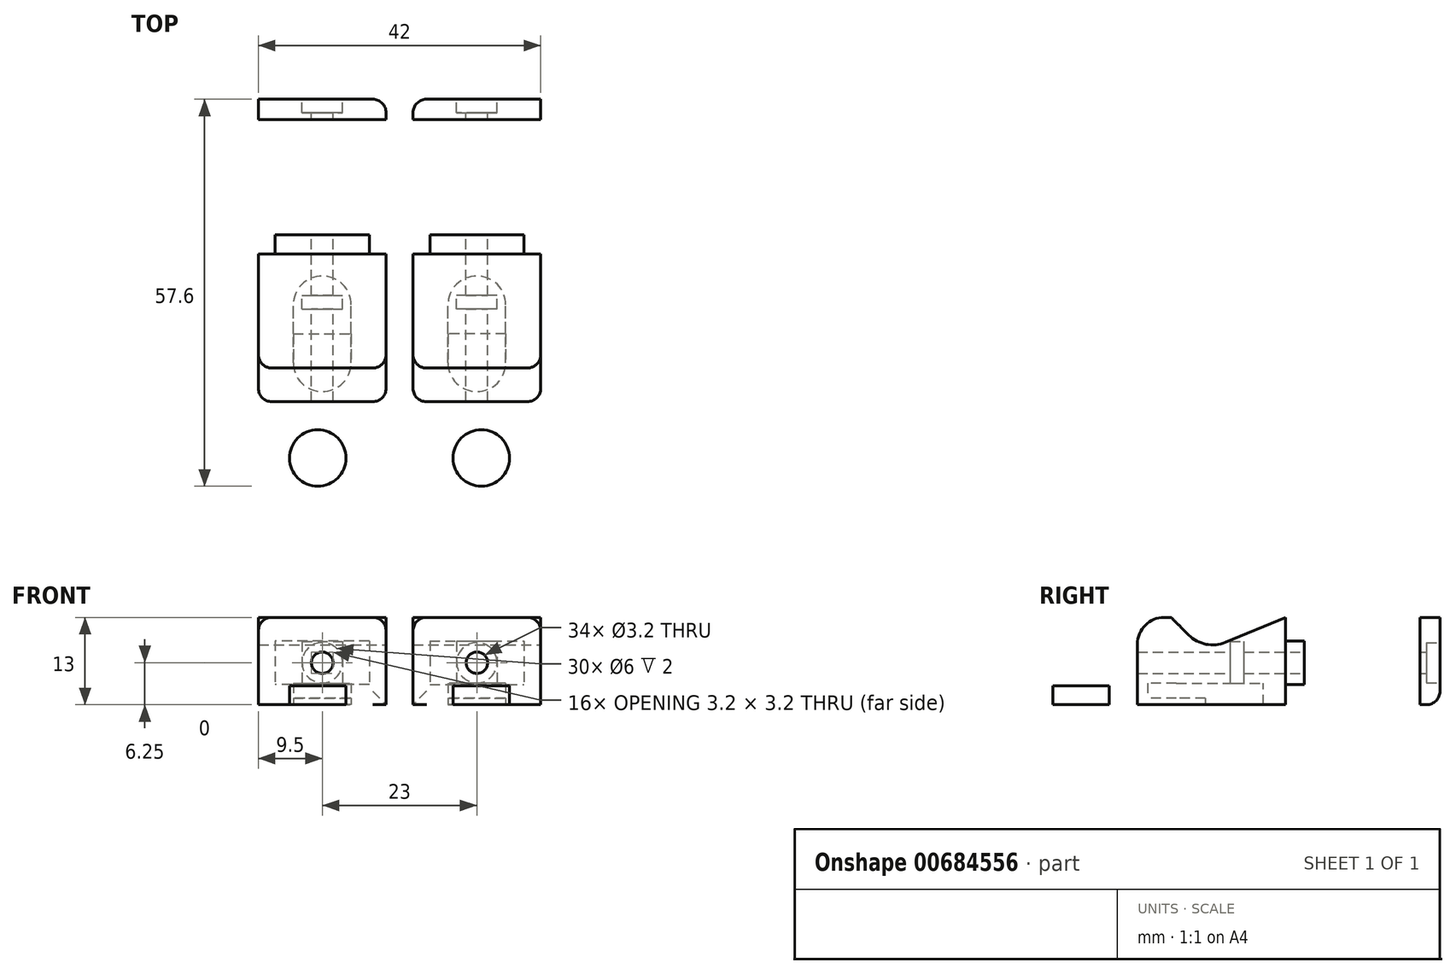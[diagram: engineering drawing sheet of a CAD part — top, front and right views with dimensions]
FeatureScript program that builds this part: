
annotation { "Feature Type Name" : "Feature", "Feature Type Description" : "" }
export const myFeature = defineFeature(function(context is Context, id is Id, definition is map)
    precondition{}
    {
        {
            var Q0;
            Q0=qCreatedBy(makeId("Top.planeOp"),FACE);
            var sketch = newSketch(context, id + "F0", { "sketchPlane" : qUnion([Q0])});
            skLineSegment(sketch, "E0.bottom", {"start": v(-2, 0) * mm, "end": v(-21, 0) * mm});
            skLineSegment(sketch, "E0.top", {"start": v(-2, -22) * mm, "end": v(-21, -22) * mm});
            skLineSegment(sketch, "E0.left", {"start": v(-2, 0) * mm, "end": v(-2, -22) * mm});
            skLineSegment(sketch, "E0.right", {"start": v(-21, 0) * mm, "end": v(-21, -22) * mm});
            skSolve(sketch);
        }
        {
            var Q0;
            Q0=makeQuery(id+"F0.imprint","IMPRINT",FACE,{"disambiguationData":[TD([[makeQuery(id+"F0.imprint","IMPRINT",EDGE,{"derivedFrom":sQuery(id+"F0.wireOp",EDGE,"E0.bottom")}),1.0]])]});
            extrude(context, id + "F1", {"entities" : qUnion([Q0]), "depth" : 13 * mm, "offsetDistance" : 25 * mm});
        }
        {
            var Q0;
            Q0=makeQuery(id+"F1.opExtrude","SWEPT_FACE",FACE,{"disambiguationData":[OSD([sQuery(id+"F0.wireOp",EDGE,"E0.right")])]});
            var sketch = newSketch(context, id + "F2", { "sketchPlane" : qUnion([Q0])});
            skLineSegment(sketch, "E1", {"start": v(0, 13) * mm, "end": v(12, 8) * mm});
            skLineSegment(sketch, "E2", {"start": v(12, 8) * mm, "end": v(17, 13) * mm});
            skSolve(sketch);
        }
        {
            var Q0;
            {var subQ0=sQuery(id+"F2.wireOp",EDGE,"E1");Q0=makeQuery(id+"F2.imprint","IMPRINT",FACE,{"disambiguationData":[TD([[makeQuery(id+"F2.imprint","IMPRINT",EDGE,{"derivedFrom":subQ0}),1.0]])]});}
            extrude(context, id + "F3", {"entities" : qUnion([Q0]), "operationType" : NewBodyOperationType.REMOVE, "endBound" : BoundingType.THROUGH_ALL, "oppositeDirection" : true, "depth" : 25 * mm, "offsetDistance" : 25 * mm});
        }
        {
            var Q0;
            Q0=makeQuery(id+"F3.boolean.opBoolean","COPY",EDGE,{"derivedFrom":makeQuery(id+"F3.opExtrude","SWEPT_EDGE",EDGE,{"disambiguationData":[OSD([sQuery(id+"F2.wireOp",EDGE,"E1"),sQuery(id+"F2.wireOp",EDGE,"E2")])]})});
            fillet(context, id + "F4", {"entities" : qUnion([Q0]), "radius" : 5 * mm, "tangentPropagation" : true, "allowEdgeOverflow" : false});
        }
        {
            var Q0;
            Q0=makeQuery(id+"F3.boolean.opBoolean","COPY",EDGE,{"derivedFrom":makeQuery(id+"F3.opExtrude","SWEPT_EDGE",EDGE,{"disambiguationData":[OSD([sQuery(id+"F0.wireOp",EDGE,"E0.right"),sQuery(id+"F2.wireOp",EDGE,"E2")])]})});
            var Q1;
            Q1=makeQuery(id+"F1.opExtrude","CAP_EDGE",EDGE,{"disambiguationData":[OSD([sQuery(id+"F0.wireOp",EDGE,"E0.top")])],"isStart":false});
            fillet(context, id + "F5", {"entities" : qUnion([Q0, Q1]), "radius" : 4 * mm, "tangentPropagation" : true, "allowEdgeOverflow" : false});
        }
        {
            var Q0;
            Q0=makeQuery(id+"F1.opExtrude","SWEPT_EDGE",EDGE,{"disambiguationData":[OSD([sQuery(id+"F0.wireOp",EDGE,"E0.top"),sQuery(id+"F0.wireOp",EDGE,"E0.right")])]});
            var Q1;
            {var subQ0=sQuery(id+"F0.wireOp",EDGE,"E0.right");Q1=makeQuery(id+"F5.opFillet","BLEND_EDGE",EDGE,{"blendedFrom":[makeQuery(id+"F3.boolean.opBoolean","COPY",EDGE,{"derivedFrom":makeQuery(id+"F3.opExtrude","SWEPT_EDGE",EDGE,{"disambiguationData":[OSD([subQ0,sQuery(id+"F2.wireOp",EDGE,"E2")])]})}),makeQuery(id+"F1.opExtrude","SWEPT_FACE",FACE,{"disambiguationData":[OSD([subQ0])]})],"blendedInto":[makeQuery(id+"F1.opExtrude","SWEPT_FACE",FACE,{"disambiguationData":[OSD([subQ0])]})]});}
            var Q2;
            Q2=makeQuery(id+"F5.opFillet","BLEND_EDGE",EDGE,{"blendedFrom":[makeQuery(id+"F1.opExtrude","CAP_EDGE",EDGE,{"disambiguationData":[OSD([sQuery(id+"F0.wireOp",EDGE,"E0.top")])],"isStart":false}),makeQuery(id+"F1.opExtrude","SWEPT_FACE",FACE,{"disambiguationData":[OSD([sQuery(id+"F0.wireOp",EDGE,"E0.left")])]})],"blendedInto":[makeQuery(id+"F1.opExtrude","SWEPT_FACE",FACE,{"disambiguationData":[OSD([sQuery(id+"F0.wireOp",EDGE,"E0.left")])]})]});
            var Q3;
            Q3=makeQuery(id+"F1.opExtrude","SWEPT_EDGE",EDGE,{"disambiguationData":[OSD([sQuery(id+"F0.wireOp",EDGE,"E0.top"),sQuery(id+"F0.wireOp",EDGE,"E0.left")])]});
            var Q4;
            Q4=makeQuery(id+"F5.opFillet","BLEND_EDGE",EDGE,{"blendedFrom":[makeQuery(id+"F3.boolean.opBoolean","COPY",EDGE,{"derivedFrom":makeQuery(id+"F3.opExtrude","SWEPT_EDGE",EDGE,{"disambiguationData":[OSD([sQuery(id+"F0.wireOp",EDGE,"E0.right"),sQuery(id+"F2.wireOp",EDGE,"E2")])]})}),makeQuery(id+"F1.opExtrude","SWEPT_FACE",FACE,{"disambiguationData":[OSD([sQuery(id+"F0.wireOp",EDGE,"E0.left")])]})],"blendedInto":[makeQuery(id+"F1.opExtrude","SWEPT_FACE",FACE,{"disambiguationData":[OSD([sQuery(id+"F0.wireOp",EDGE,"E0.left")])]})]});
            fillet(context, id + "F6", {"entities" : qUnion([Q0, Q1, Q2, Q3, Q4]), "radius" : 2 * mm, "tangentPropagation" : true, "allowEdgeOverflow" : false});
        }
        {
            var Q0;
            Q0=makeQuery(id+"F1.opExtrude","SWEPT_FACE",FACE,{"disambiguationData":[OSD([sQuery(id+"F0.wireOp",EDGE,"E0.bottom")])]});
            extrude(context, id + "F7", {"entities" : qUnion([Q0]), "depth" : 3 * mm, "offsetDistance" : 25 * mm});
        }
        {
            var Q0;
            Q0=makeQuery(id+"F7.opExtrude","SWEPT_BODY",BODY,{"disambiguationData":[OSD([sQuery(id+"F0.wireOp",EDGE,"E0.bottom")])]});
            transform(context, id + "F8", {"entities" : qUnion([Q0]), "transformType" : TransformType.TRANSLATION_3D, "dx" : 0 * mm, "dy" : 20 * mm, "dz" : 0 * mm, "makeCopy" : false});
        }
        {
            var Q0;
            Q0=makeQuery(id+"F1.opExtrude","SWEPT_FACE",FACE,{"disambiguationData":[OSD([sQuery(id+"F0.wireOp",EDGE,"E0.bottom")])]});
            var sketch = newSketch(context, id + "F9", { "sketchPlane" : qUnion([Q0])});
            skLineSegment(sketch, "E3.bottom", {"start": v(4.5, 9.5) * mm, "end": v(18.5, 9.5) * mm});
            skLineSegment(sketch, "E3.top", {"start": v(4.5, 3) * mm, "end": v(18.5, 3) * mm});
            skLineSegment(sketch, "E3.left", {"start": v(4.5, 9.5) * mm, "end": v(4.5, 3) * mm});
            skLineSegment(sketch, "E3.right", {"start": v(18.5, 9.5) * mm, "end": v(18.5, 3) * mm});
            skSolve(sketch);
        }
        {
            var Q0;
            Q0=makeQuery(id+"F9.imprint","IMPRINT",FACE,{"disambiguationData":[TD([[makeQuery(id+"F9.imprint","IMPRINT",EDGE,{"derivedFrom":sQuery(id+"F9.wireOp",EDGE,"E3.bottom")}),-1.0]])]});
            extrude(context, id + "F10", {"entities" : qUnion([Q0]), "operationType" : NewBodyOperationType.ADD, "depth" : 2.8 * mm, "offsetDistance" : 25 * mm});
        }
        {
            var Q0;
            Q0=makeQuery(id+"F10.opExtrude","CAP_FACE",FACE,{"disambiguationData":[OSD([sQuery(id+"F9.wireOp",EDGE,"E3.bottom"),sQuery(id+"F9.wireOp",EDGE,"E3.top"),sQuery(id+"F9.wireOp",EDGE,"E3.left"),sQuery(id+"F9.wireOp",EDGE,"E3.right")])],"isStart":false});
            var sketch = newSketch(context, id + "F11", { "sketchPlane" : qUnion([Q0])});
            skCircle(sketch, "E4", {"center": v(11.5, 6.25) * mm, "radius": 1.6 * mm});
            skSolve(sketch);
        }
        {
            var Q0;
            Q0=makeQuery(id+"F11.imprint","IMPRINT",FACE,{"disambiguationData":[TD([[makeQuery(id+"F11.imprint","IMPRINT",EDGE,{"derivedFrom":sQuery(id+"F11.wireOp",EDGE,"E4")}),1.0]])]});
            extrude(context, id + "F12", {"entities" : qUnion([Q0]), "operationType" : NewBodyOperationType.REMOVE, "oppositeDirection" : true, "depth" : 20 * mm, "offsetDistance" : 25 * mm});
        }
        {
            var Q0;
            Q0=makeQuery(id+"F1.opExtrude","CAP_FACE",FACE,{"disambiguationData":[OSD([sQuery(id+"F0.wireOp",EDGE,"E0.bottom"),sQuery(id+"F0.wireOp",EDGE,"E0.top"),sQuery(id+"F0.wireOp",EDGE,"E0.left"),sQuery(id+"F0.wireOp",EDGE,"E0.right")])],"isStart":true});
            var sketch = newSketch(context, id + "F13", { "sketchPlane" : qUnion([Q0])});
            skLineSegment(sketch, "E5.bottom", {"start": v(-15.8, 20.5) * mm, "end": v(-7.2, 20.5) * mm});
            skLineSegment(sketch, "E5.top", {"start": v(-15.8, 3.3) * mm, "end": v(-7.2, 3.3) * mm});
            skLineSegment(sketch, "E5.left", {"start": v(-15.8, 20.5) * mm, "end": v(-15.8, 3.3) * mm});
            skLineSegment(sketch, "E5.right", {"start": v(-7.2, 20.5) * mm, "end": v(-7.2, 3.3) * mm});
            skSolve(sketch);
        }
        {
            var Q0;
            Q0=makeQuery(id+"F13.imprint","IMPRINT",FACE,{"disambiguationData":[TD([[makeQuery(id+"F13.imprint","IMPRINT",EDGE,{"derivedFrom":sQuery(id+"F13.wireOp",EDGE,"E5.bottom")}),-1.0]])]});
            extrude(context, id + "F14", {"entities" : qUnion([Q0]), "operationType" : NewBodyOperationType.REMOVE, "oppositeDirection" : true, "depth" : 3.2 * mm, "offsetDistance" : 25 * mm});
        }
        {
            var Q0;
            Q0=makeQuery(id+"F14.boolean.opBoolean","COPY",FACE,{"derivedFrom":makeQuery(id+"F14.opExtrude","SWEPT_FACE",FACE,{"disambiguationData":[OSD([sQuery(id+"F13.wireOp",EDGE,"E5.bottom")])]})});
            var sketch = newSketch(context, id + "F15", { "sketchPlane" : qUnion([Q0])});
            skLineSegment(sketch, "E6.bottom", {"start": v(15.8, 0) * mm, "end": v(7.2, 0) * mm});
            skLineSegment(sketch, "E6.top", {"start": v(15.8, 1) * mm, "end": v(7.2, 1) * mm});
            skLineSegment(sketch, "E6.left", {"start": v(15.8, 0) * mm, "end": v(15.8, 1) * mm});
            skLineSegment(sketch, "E6.right", {"start": v(7.2, 0) * mm, "end": v(7.2, 1) * mm});
            skSolve(sketch);
        }
        {
            var Q0;
            Q0=makeQuery(id+"F15.imprint","IMPRINT",FACE,{"disambiguationData":[TD([[makeQuery(id+"F15.imprint","IMPRINT",EDGE,{"derivedFrom":sQuery(id+"F15.wireOp",EDGE,"E6.bottom")}),-1.0]])]});
            extrude(context, id + "F16", {"entities" : qUnion([Q0]), "operationType" : NewBodyOperationType.ADD, "depth" : 8.6 * mm, "offsetDistance" : 25 * mm});
        }
        {
            var Q0;
            Q0=makeQuery(id+"F14.boolean.opBoolean","COPY",EDGE,{"derivedFrom":makeQuery(id+"F14.opExtrude","SWEPT_EDGE",EDGE,{"disambiguationData":[OSD([sQuery(id+"F13.wireOp",EDGE,"E5.bottom"),sQuery(id+"F13.wireOp",EDGE,"E5.left")])]})});
            var Q1;
            Q1=makeQuery(id+"F14.boolean.opBoolean","COPY",EDGE,{"derivedFrom":makeQuery(id+"F14.opExtrude","SWEPT_EDGE",EDGE,{"disambiguationData":[OSD([sQuery(id+"F13.wireOp",EDGE,"E5.bottom"),sQuery(id+"F13.wireOp",EDGE,"E5.right")])]})});
            var Q2;
            Q2=makeQuery(id+"F16.opExtrude","CAP_EDGE",EDGE,{"disambiguationData":[OSD([sQuery(id+"F15.wireOp",EDGE,"E6.left")])],"isStart":false});
            var Q3;
            Q3=makeQuery(id+"F16.opExtrude","CAP_EDGE",EDGE,{"disambiguationData":[OSD([sQuery(id+"F15.wireOp",EDGE,"E6.right")])],"isStart":false});
            var Q4;
            Q4=makeQuery(id+"F14.boolean.opBoolean","COPY",EDGE,{"derivedFrom":makeQuery(id+"F14.opExtrude","SWEPT_EDGE",EDGE,{"disambiguationData":[OSD([sQuery(id+"F13.wireOp",EDGE,"E5.top"),sQuery(id+"F13.wireOp",EDGE,"E5.left")])]})});
            var Q5;
            Q5=makeQuery(id+"F14.boolean.opBoolean","COPY",EDGE,{"derivedFrom":makeQuery(id+"F14.opExtrude","SWEPT_EDGE",EDGE,{"disambiguationData":[OSD([sQuery(id+"F13.wireOp",EDGE,"E5.top"),sQuery(id+"F13.wireOp",EDGE,"E5.right")])]})});
            fillet(context, id + "F17", {"entities" : qUnion([Q0, Q1, Q2, Q3, Q4, Q5]), "radius" : 4.3 * mm, "tangentPropagation" : true, "allowEdgeOverflow" : false});
        }
        {
            var Q0;
            Q0=makeQuery(id+"F14.boolean.opBoolean","COPY",FACE,{"derivedFrom":makeQuery(id+"F14.opExtrude","CAP_FACE",FACE,{"disambiguationData":[OSD([sQuery(id+"F13.wireOp",EDGE,"E5.bottom"),sQuery(id+"F13.wireOp",EDGE,"E5.top"),sQuery(id+"F13.wireOp",EDGE,"E5.left"),sQuery(id+"F13.wireOp",EDGE,"E5.right")])],"isStart":false})});
            var sketch = newSketch(context, id + "F18", { "sketchPlane" : qUnion([Q0])});
            skLineSegment(sketch, "E7.bottom", {"start": v(-14.5, 8.2) * mm, "end": v(-8.5, 8.2) * mm});
            skLineSegment(sketch, "E7.top", {"start": v(-14.5, 6.2) * mm, "end": v(-8.5, 6.2) * mm});
            skLineSegment(sketch, "E7.left", {"start": v(-14.5, 8.2) * mm, "end": v(-14.5, 6.2) * mm});
            skLineSegment(sketch, "E7.right", {"start": v(-8.5, 8.2) * mm, "end": v(-8.5, 6.2) * mm});
            skSolve(sketch);
        }
        {
            var Q0;
            Q0=makeQuery(id+"F18.imprint","IMPRINT",FACE,{"disambiguationData":[TD([[makeQuery(id+"F18.imprint","IMPRINT",EDGE,{"derivedFrom":sQuery(id+"F18.wireOp",EDGE,"E7.bottom")}),-1.0]])]});
            extrude(context, id + "F19", {"entities" : qUnion([Q0]), "operationType" : NewBodyOperationType.REMOVE, "oppositeDirection" : true, "depth" : 6.2 * mm, "offsetDistance" : 25 * mm});
        }
        {
            var Q0;
            Q0=makeQuery(id+"F7.opExtrude","CAP_FACE",FACE,{"disambiguationData":[OSD([sQuery(id+"F0.wireOp",EDGE,"E0.bottom")])],"isStart":false});
            var sketch = newSketch(context, id + "F20", { "sketchPlane" : qUnion([Q0])});
            skCircle(sketch, "E8", {"center": v(11.5, 6.25) * mm, "radius": 1.6 * mm});
            skSolve(sketch);
        }
        {
            var Q0;
            Q0=makeQuery(id+"F20.imprint","IMPRINT",FACE,{"disambiguationData":[TD([[makeQuery(id+"F20.imprint","IMPRINT",EDGE,{"derivedFrom":sQuery(id+"F20.wireOp",EDGE,"E8")}),1.0]])]});
            extrude(context, id + "F21", {"entities" : qUnion([Q0]), "operationType" : NewBodyOperationType.REMOVE, "endBound" : BoundingType.THROUGH_ALL, "oppositeDirection" : true, "depth" : 25 * mm, "offsetDistance" : 25 * mm});
        }
        {
            var Q0;
            Q0=makeQuery(id+"F7.opExtrude","CAP_FACE",FACE,{"disambiguationData":[OSD([sQuery(id+"F0.wireOp",EDGE,"E0.bottom")])],"isStart":false});
            var sketch = newSketch(context, id + "F22", { "sketchPlane" : qUnion([Q0])});
            skCircle(sketch, "E9", {"center": v(11.5, 6.25) * mm, "radius": 3 * mm});
            skSolve(sketch);
        }
        {
            var Q0;
            Q0=makeQuery(id+"F22.imprint","IMPRINT",FACE,{"disambiguationData":[TD([[makeQuery(id+"F22.imprint","IMPRINT",EDGE,{"derivedFrom":sQuery(id+"F22.wireOp",EDGE,"E9")}),1.0]])]});
            extrude(context, id + "F23", {"entities" : qUnion([Q0]), "operationType" : NewBodyOperationType.REMOVE, "oppositeDirection" : true, "depth" : 2 * mm, "offsetDistance" : 25 * mm});
        }
        {
            var Q0;
            Q0=makeQuery(id+"F7.opExtrude","CAP_EDGE",EDGE,{"disambiguationData":[OSD([sQuery(id+"F0.wireOp",EDGE,"E0.bottom"),sQuery(id+"F0.wireOp",EDGE,"E0.left")])],"isStart":false});
            var Q1;
            Q1=makeQuery(id+"F7.opExtrude","CAP_EDGE",EDGE,{"disambiguationData":[OSD([sQuery(id+"F0.wireOp",EDGE,"E0.bottom")])],"isStart":false});
            fillet(context, id + "F24", {"entities" : qUnion([Q0, Q1]), "radius" : 2 * mm, "tangentPropagation" : true, "allowEdgeOverflow" : false});
        }
        {
            var Q0;
            Q0=makeQuery(id+"F1.opExtrude","SWEPT_BODY",BODY,{"disambiguationData":[OSD([sQuery(id+"F0.wireOp",EDGE,"E0.bottom"),sQuery(id+"F0.wireOp",EDGE,"E0.top"),sQuery(id+"F0.wireOp",EDGE,"E0.left"),sQuery(id+"F0.wireOp",EDGE,"E0.right")])]});
            var Q1;
            Q1=makeQuery(id+"F7.opExtrude","SWEPT_BODY",BODY,{"disambiguationData":[OSD([sQuery(id+"F0.wireOp",EDGE,"E0.bottom")])]});
            var Q2;
            Q2=qCreatedBy(makeId("Right.planeOp"),FACE);
            mirror(context, id + "F25", {"entities" : qUnion([Q0, Q1]), "mirrorPlane" : qUnion([Q2])});
        }
        {
            var Q0;
            Q0=qCreatedBy(makeId("Top.planeOp"),FACE);
            var sketch = newSketch(context, id + "F26", { "sketchPlane" : qUnion([Q0])});
            skCircle(sketch, "E10", {"center": v(-12.17, -30.4) * mm, "radius": 4.2 * mm});
            skSolve(sketch);
        }
        {
            var Q0;
            Q0=makeQuery(id+"F26.imprint","IMPRINT",FACE,{"disambiguationData":[TD([[makeQuery(id+"F26.imprint","IMPRINT",EDGE,{"derivedFrom":sQuery(id+"F26.wireOp",EDGE,"E10")}),1.0]])]});
            extrude(context, id + "F27", {"entities" : qUnion([Q0]), "depth" : 2.8 * mm, "offsetDistance" : 25 * mm});
        }
        {
            var Q0;
            Q0=makeQuery(id+"F27.opExtrude","SWEPT_BODY",BODY,{"disambiguationData":[OSD([sQuery(id+"F26.wireOp",EDGE,"E10")])]});
            var Q1;
            Q1=qCreatedBy(makeId("Right.planeOp"),FACE);
            mirror(context, id + "F28", {"entities" : qUnion([Q0]), "mirrorPlane" : qUnion([Q1])});
        }
    });
